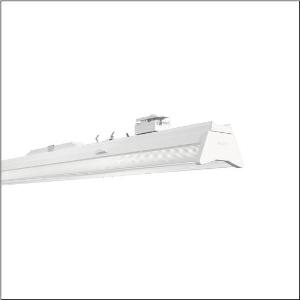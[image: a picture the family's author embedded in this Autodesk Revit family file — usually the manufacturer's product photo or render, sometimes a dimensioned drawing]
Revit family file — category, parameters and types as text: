
# Revit family: licross_r__11_performance_ho_51td16mn4gxm_b838
name_source: partatom
category: Lighting Fixtures
units: mm (PartAtom-declared; Revit-internal decimal feet)

## family parameters
Cut with Voids When Loaded = No
Host = Face
Light Source = No
Part Type = Normal
Room Calculation Point = No
Round Connector Dimension = Use Diameter
Shared = No

## types (1)
- --- (1 x LED, 16020 lm, 87.4 W, 4000K)
    Apparent Load = 87 VA
    CIE Flux Codes = 63 87 95 78 100
    Color Rendering = 80
    Color Temperature = 4000K
    Default Elevation = 1800 mm
    Description = Licross® 11 Performance HO, luminaire insert, of sheet steel, galvanised, coil coated, white, length: 1.500mm, width: 120mm, height: 123mm, LED rated luminous flux: 16.020lm, light colour: 840, control gear: ON/OFF Multilumen, with plug, 3-pole, with phase selection, mains connection: 220..240V, AC, 50/60Hz, rated input power: 87W, halogen-free wiring, primary light control with lens, of plastic, primary optical cover: cover, of PMMA, light emission: direct/indirect distribution, primary light characteristic: symmetric, protection rating (complete): IP54, insulation class (complete): insulation class I (protective earthing), certification: CE, ENEC, VDE, UKCA, protection symbol: D if used in an environment with non-conductive dust loads with corresponding accessories, impact resistance: IK06, permissible ambient temperature for indoor applications: -35..+35°C, corresponds to IFS (International Featured Standards) requirements for safety and quality in the food industry, reducing of maximum allowable ambient temperature of 5°C with ceiling mounting, LABS conformity tested according to VDMA 24364:2018-05, packaging unit: 1 piece
    Height = 114 mm
    Lamp = 1 x LED
    Lamp Light Flux = 16020 lm
    Lamp Power = 87.4 W
    Lamp count = 1
    Length = 1500 mm
    Luminous efficacy = 183 lm/W
    Manufacturer = Siteco
    ModVariant = No
    Model = 51TD16MN4GXM
    Mounting Place = Ceiling
    Mounting Type = Pendant
    Number of Poles = 1
    OnlyDefault = Yes
    Power Factor = 1
    Product Name = Licross® 11 Performance HO
    Product group = luminaire insert
    ProductGroupID = 901
    Protection Class = Protection class I
    Protection Degree = IP 54
    RLX_Detail_Level = 1
    RLX_Emergency_Light_Flux = 0 lm
    RLX_Emergency_Type = 0
    RLX_Emergency_Type_DB = No
    RlxData = <blob elided: 31749 chars, md5=efd5937a>
    Socket = socket
    Standby Power = 0 W
    System Light Flux = 16020 lm
    System Power = 87 W
    Type Comments = factory setting: luminous flux: 100 % | (A | C | E) | 203 mA
    Type Image = l_1256138.jpg
    URL = http://relux.com
    VarID = @adj_038371
    Voltage = 0 V
    Weight = 0.00 kg
    Width = 120 mm

## geometry (parser evidence)
native form markers: Blend x4, Sweep x11
no freeform markers — native parametric forms only
